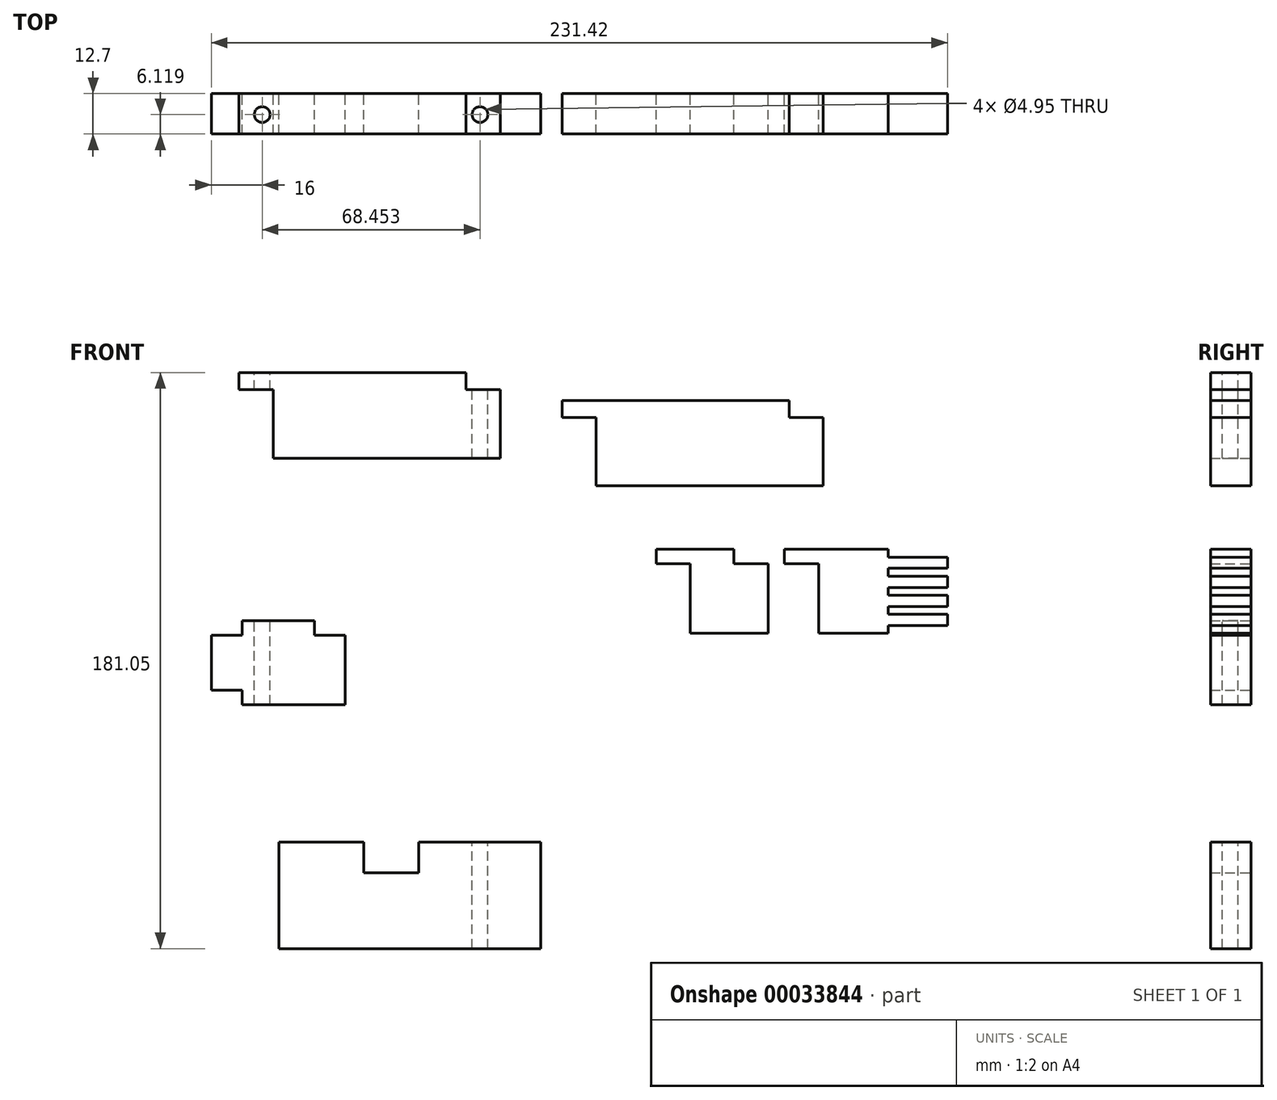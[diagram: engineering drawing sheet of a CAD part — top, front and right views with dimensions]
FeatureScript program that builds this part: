
annotation { "Feature Type Name" : "Feature", "Feature Type Description" : "" }
export const myFeature = defineFeature(function(context is Context, id is Id, definition is map)
    precondition{}
    {
        {
            var Q0;
            Q0=qCreatedBy(makeId("Front.planeOp"),FACE);
            var sketch = newSketch(context, id + "F0", { "sketchPlane" : qUnion([Q0])});
            skLineSegment(sketch, "E0.bottom", {"start": v(-99.87, -47.6) * mm, "end": v(-17.62, -47.6) * mm});
            skLineSegment(sketch, "E0.top", {"start": v(-99.87, -81.14) * mm, "end": v(-17.62, -81.14) * mm});
            skLineSegment(sketch, "E0.left", {"start": v(-99.87, -47.6) * mm, "end": v(-99.87, -81.14) * mm});
            skLineSegment(sketch, "E0.right", {"start": v(-17.62, -47.6) * mm, "end": v(-17.62, -81.14) * mm});
            skLineSegment(sketch, "E1.bottom", {"start": v(-112.5, 99.9) * mm, "end": v(-30.38, 99.9) * mm});
            skLineSegment(sketch, "E1.top", {"start": v(-112.5, 73.05) * mm, "end": v(-30.38, 73.05) * mm});
            skLineSegment(sketch, "E1.left", {"start": v(-112.5, 99.9) * mm, "end": v(-112.5, 73.05) * mm});
            skLineSegment(sketch, "E1.right", {"start": v(-30.38, 99.9) * mm, "end": v(-30.38, 73.05) * mm});
            skLineSegment(sketch, "E2", {"start": v(-112.5, 94.54) * mm, "end": v(-101.75, 94.54) * mm});
            skLineSegment(sketch, "E3", {"start": v(-101.75, 94.54) * mm, "end": v(-101.75, 77.27) * mm});
            skLineSegment(sketch, "E4", {"start": v(-101.75, 77.27) * mm, "end": v(-112.5, 77.27) * mm});
            skLineSegment(sketch, "E5", {"start": v(-30.38, 94.54) * mm, "end": v(-41.12, 94.54) * mm});
            skLineSegment(sketch, "E6", {"start": v(-41.12, 94.54) * mm, "end": v(-41.12, 77.27) * mm});
            skLineSegment(sketch, "E7", {"start": v(-41.12, 77.27) * mm, "end": v(-30.38, 77.27) * mm});
            skLineSegment(sketch, "E8.bottom", {"start": v(1.68, -53.97) * mm, "end": v(83.93, -53.97) * mm});
            skLineSegment(sketch, "E8.top", {"start": v(1.68, -87.5) * mm, "end": v(83.93, -87.5) * mm});
            skLineSegment(sketch, "E8.left", {"start": v(1.68, -53.97) * mm, "end": v(1.68, -87.5) * mm});
            skLineSegment(sketch, "E8.right", {"start": v(83.93, -53.97) * mm, "end": v(83.93, -87.5) * mm});
            skLineSegment(sketch, "E9.bottom", {"start": v(-10.94, 91.2) * mm, "end": v(71.17, 91.2) * mm});
            skLineSegment(sketch, "E9.top", {"start": v(-10.94, 64.34) * mm, "end": v(71.17, 64.34) * mm});
            skLineSegment(sketch, "E9.left", {"start": v(-10.94, 91.2) * mm, "end": v(-10.94, 64.34) * mm});
            skLineSegment(sketch, "E9.right", {"start": v(71.17, 91.2) * mm, "end": v(71.17, 64.34) * mm});
            skLineSegment(sketch, "E10", {"start": v(-10.94, 85.82) * mm, "end": v(-0.2, 85.82) * mm});
            skLineSegment(sketch, "E11", {"start": v(-0.2, 85.82) * mm, "end": v(-0.2, 68.56) * mm});
            skLineSegment(sketch, "E12", {"start": v(-0.2, 68.56) * mm, "end": v(-10.94, 68.56) * mm});
            skLineSegment(sketch, "E13", {"start": v(71.17, 85.82) * mm, "end": v(60.43, 85.82) * mm});
            skLineSegment(sketch, "E14", {"start": v(60.43, 85.82) * mm, "end": v(60.43, 68.56) * mm});
            skLineSegment(sketch, "E15", {"start": v(60.43, 68.56) * mm, "end": v(71.17, 68.56) * mm});
            skLineSegment(sketch, "E16.bottom", {"start": v(-111.54, 21.96) * mm, "end": v(-88.82, 21.96) * mm});
            skLineSegment(sketch, "E16.top", {"start": v(-111.54, -4.45) * mm, "end": v(-88.82, -4.45) * mm});
            skLineSegment(sketch, "E16.left", {"start": v(-111.54, 21.96) * mm, "end": v(-111.54, -4.45) * mm});
            skLineSegment(sketch, "E16.right", {"start": v(-88.82, 21.96) * mm, "end": v(-88.82, -4.45) * mm});
            skLineSegment(sketch, "E17.bottom", {"start": v(-88.82, 17.4) * mm, "end": v(-79.17, 17.4) * mm});
            skLineSegment(sketch, "E17.top", {"start": v(-88.82, 0.13) * mm, "end": v(-79.17, 0.13) * mm});
            skLineSegment(sketch, "E17.left", {"start": v(-88.82, 17.4) * mm, "end": v(-88.82, 0.13) * mm});
            skLineSegment(sketch, "E17.right", {"start": v(-79.17, 17.4) * mm, "end": v(-79.17, 0.13) * mm});
            skLineSegment(sketch, "E18", {"start": v(-0.2, 91.2) * mm, "end": v(-0.2, 64.34) * mm});
            skLineSegment(sketch, "E19", {"start": v(60.43, 91.2) * mm, "end": v(60.43, 64.34) * mm});
            skLineSegment(sketch, "E20.bottom", {"start": v(18.66, 44.37) * mm, "end": v(53.82, 44.37) * mm});
            skLineSegment(sketch, "E20.top", {"start": v(18.66, 17.95) * mm, "end": v(53.82, 17.95) * mm});
            skLineSegment(sketch, "E20.left", {"start": v(18.66, 44.37) * mm, "end": v(18.66, 17.95) * mm});
            skLineSegment(sketch, "E20.right", {"start": v(53.82, 44.37) * mm, "end": v(53.82, 17.95) * mm});
            skLineSegment(sketch, "E21.bottom", {"start": v(18.66, 39.8) * mm, "end": v(29.4, 39.8) * mm});
            skLineSegment(sketch, "E21.top", {"start": v(18.66, 22.52) * mm, "end": v(29.4, 22.52) * mm});
            skLineSegment(sketch, "E21.left", {"start": v(18.66, 39.8) * mm, "end": v(18.66, 22.52) * mm});
            skLineSegment(sketch, "E21.right", {"start": v(29.4, 39.8) * mm, "end": v(29.4, 22.52) * mm});
            skLineSegment(sketch, "E22.bottom", {"start": v(53.82, 39.8) * mm, "end": v(43.08, 39.8) * mm});
            skLineSegment(sketch, "E22.top", {"start": v(53.82, 22.52) * mm, "end": v(43.08, 22.52) * mm});
            skLineSegment(sketch, "E22.left", {"start": v(53.82, 39.8) * mm, "end": v(53.82, 22.52) * mm});
            skLineSegment(sketch, "E22.right", {"start": v(43.08, 39.8) * mm, "end": v(43.08, 22.52) * mm});
            skLineSegment(sketch, "E23.bottom", {"start": v(58.98, 39.8) * mm, "end": v(69.72, 39.8) * mm});
            skLineSegment(sketch, "E23.top", {"start": v(58.98, 22.52) * mm, "end": v(69.72, 22.52) * mm});
            skLineSegment(sketch, "E23.left", {"start": v(58.98, 39.8) * mm, "end": v(58.98, 22.52) * mm});
            skLineSegment(sketch, "E23.right", {"start": v(69.72, 39.8) * mm, "end": v(69.72, 22.52) * mm});
            skLineSegment(sketch, "E24.bottom", {"start": v(69.72, 44.37) * mm, "end": v(91.55, 44.37) * mm});
            skLineSegment(sketch, "E24.top", {"start": v(69.72, 17.95) * mm, "end": v(91.55, 17.95) * mm});
            skLineSegment(sketch, "E24.left", {"start": v(69.72, 44.37) * mm, "end": v(69.72, 17.95) * mm});
            skLineSegment(sketch, "E24.right", {"start": v(91.55, 44.37) * mm, "end": v(91.55, 17.95) * mm});
            skLineSegment(sketch, "E25.left", {"start": v(91.55, 44.37) * mm, "end": v(91.55, 38.1) * mm});
            skLineSegment(sketch, "E26.left", {"start": v(91.55, 32.2) * mm, "end": v(91.55, 28.51) * mm});
            skLineSegment(sketch, "E27.left", {"start": v(91.55, 23.69) * mm, "end": v(91.55, 20) * mm});
            skLineSegment(sketch, "E28.bottom", {"start": v(81.37, 17.95) * mm, "end": v(77.1, 17.95) * mm});
            skLineSegment(sketch, "E28.top", {"start": v(81.37, 9.97) * mm, "end": v(77.1, 9.97) * mm});
            skLineSegment(sketch, "E28.left", {"start": v(81.37, 17.95) * mm, "end": v(81.37, 9.97) * mm});
            skLineSegment(sketch, "E28.right", {"start": v(77.1, 17.95) * mm, "end": v(77.1, 9.97) * mm});
            skLineSegment(sketch, "E29.bottom", {"start": v(-111.54, 17.4) * mm, "end": v(-121.19, 17.4) * mm});
            skLineSegment(sketch, "E29.top", {"start": v(-111.54, 0.13) * mm, "end": v(-121.19, 0.13) * mm});
            skLineSegment(sketch, "E29.left", {"start": v(-111.54, 17.4) * mm, "end": v(-111.54, 0.13) * mm});
            skLineSegment(sketch, "E29.right", {"start": v(-121.19, 17.4) * mm, "end": v(-121.19, 0.13) * mm});
            skLineSegment(sketch, "E30.bottom", {"start": v(-73.2, -47.6) * mm, "end": v(-55.93, -47.6) * mm});
            skLineSegment(sketch, "E30.top", {"start": v(-73.2, -57.26) * mm, "end": v(-55.93, -57.26) * mm});
            skLineSegment(sketch, "E30.left", {"start": v(-73.2, -47.6) * mm, "end": v(-73.2, -57.26) * mm});
            skLineSegment(sketch, "E30.right", {"start": v(-55.93, -47.6) * mm, "end": v(-55.93, -57.26) * mm});
            skLineSegment(sketch, "E31.bottom", {"start": v(91.55, 41.9) * mm, "end": v(110.23, 41.9) * mm});
            skLineSegment(sketch, "E31.top", {"start": v(91.55, 38.38) * mm, "end": v(110.23, 38.38) * mm});
            skLineSegment(sketch, "E31.left", {"start": v(91.55, 41.9) * mm, "end": v(91.55, 38.38) * mm});
            skLineSegment(sketch, "E31.right", {"start": v(110.23, 41.9) * mm, "end": v(110.23, 38.38) * mm});
            skLineSegment(sketch, "E32.bottom", {"start": v(91.55, 35.91) * mm, "end": v(110.23, 35.91) * mm});
            skLineSegment(sketch, "E32.top", {"start": v(91.55, 32.4) * mm, "end": v(110.23, 32.4) * mm});
            skLineSegment(sketch, "E32.left", {"start": v(91.55, 35.91) * mm, "end": v(91.55, 32.4) * mm});
            skLineSegment(sketch, "E32.right", {"start": v(110.23, 35.91) * mm, "end": v(110.23, 32.4) * mm});
            skLineSegment(sketch, "E33.bottom", {"start": v(91.55, 29.93) * mm, "end": v(110.23, 29.93) * mm});
            skLineSegment(sketch, "E33.top", {"start": v(91.55, 26.4) * mm, "end": v(110.23, 26.4) * mm});
            skLineSegment(sketch, "E33.left", {"start": v(91.55, 29.93) * mm, "end": v(91.55, 26.4) * mm});
            skLineSegment(sketch, "E33.right", {"start": v(110.23, 29.93) * mm, "end": v(110.23, 26.4) * mm});
            skLineSegment(sketch, "E34.bottom", {"start": v(91.55, 20.42) * mm, "end": v(110.23, 20.42) * mm});
            skLineSegment(sketch, "E34.top", {"start": v(91.55, 23.94) * mm, "end": v(110.23, 23.94) * mm});
            skLineSegment(sketch, "E34.left", {"start": v(91.55, 20.42) * mm, "end": v(91.55, 23.94) * mm});
            skLineSegment(sketch, "E34.right", {"start": v(110.23, 20.42) * mm, "end": v(110.23, 23.94) * mm});
            skLineSegment(sketch, "E35", {"start": v(91.55, 44.37) * mm, "end": v(91.55, 41.9) * mm});
            skLineSegment(sketch, "E36", {"start": v(91.55, 38.38) * mm, "end": v(91.55, 35.91) * mm});
            skLineSegment(sketch, "E37", {"start": v(91.55, 32.4) * mm, "end": v(91.55, 29.93) * mm});
            skLineSegment(sketch, "E38", {"start": v(91.55, 26.4) * mm, "end": v(91.55, 23.94) * mm});
            skLineSegment(sketch, "E39", {"start": v(91.55, 20.42) * mm, "end": v(91.55, 17.95) * mm});
            skPoint(sketch, "E40.startSnap0", {"position": v(24.03, 39.8) * mm});
            skPoint(sketch, "E41.startSnap0", {"position": v(48.45, 22.52) * mm});
            skPoint(sketch, "E42.startSnap0", {"position": v(48.45, 39.8) * mm});
            skLineSegment(sketch, "E43", {"start": v(-101.75, 99.9) * mm, "end": v(-101.75, 73.05) * mm});
            skLineSegment(sketch, "E44", {"start": v(-41.12, 99.9) * mm, "end": v(-41.12, 73.05) * mm});
            skLineSegment(sketch, "E45", {"start": v(29.4, 44.37) * mm, "end": v(29.4, 17.95) * mm});
            skLineSegment(sketch, "E46", {"start": v(43.08, 44.37) * mm, "end": v(43.08, 17.95) * mm});
            skLineSegment(sketch, "E47", {"start": v(-111.54, 21.96) * mm, "end": v(-121.19, 21.96) * mm});
            skLineSegment(sketch, "E48", {"start": v(-121.19, 21.96) * mm, "end": v(-121.19, 17.4) * mm});
            skLineSegment(sketch, "E49", {"start": v(-121.19, 0.13) * mm, "end": v(-121.19, -4.45) * mm});
            skLineSegment(sketch, "E50", {"start": v(-121.19, -4.45) * mm, "end": v(-111.54, -4.45) * mm});
            skLineSegment(sketch, "E51", {"start": v(-88.82, -4.45) * mm, "end": v(-79.17, -4.45) * mm});
            skLineSegment(sketch, "E52", {"start": v(-79.17, -4.45) * mm, "end": v(-79.17, 0.13) * mm});
            skLineSegment(sketch, "E53", {"start": v(-88.82, 21.96) * mm, "end": v(-79.17, 21.96) * mm});
            skLineSegment(sketch, "E54", {"start": v(-79.17, 21.96) * mm, "end": v(-79.17, 17.4) * mm});
            skLineSegment(sketch, "E55", {"start": v(58.98, 22.52) * mm, "end": v(58.98, 17.95) * mm});
            skLineSegment(sketch, "E56", {"start": v(58.98, 17.95) * mm, "end": v(69.72, 17.95) * mm});
            skLineSegment(sketch, "E57", {"start": v(69.72, 44.37) * mm, "end": v(58.98, 44.37) * mm});
            skLineSegment(sketch, "E58", {"start": v(58.98, 44.37) * mm, "end": v(58.98, 39.8) * mm});
            skLineSegment(sketch, "E59", {"start": v(-112.5, 99.9) * mm, "end": v(-112.5, 94.54) * mm});
            skSolve(sketch);
        }
        {
            var Q0;
            {var subQ5=sQuery(id+"F0.wireOp",EDGE,"E9.bottom");var subQ7=sQuery(id+"F0.wireOp",EDGE,"E18");var subQ10=makeQuery(id+"F0.imprint","INTERSECT",VERTEX,{"derivedFrom":[subQ5,subQ7]});Q0=makeQuery(id+"F0.imprint","IMPRINT",FACE,{"disambiguationData":[TD([[makeQuery(id+"F0.imprint","IMPRINT",EDGE,{"disambiguationData":[TD([[subQ10,-1.0]])],"derivedFrom":subQ5}),-1.0]])]});}
            var Q1;
            {var subQ3=sQuery(id+"F0.wireOp",EDGE,"E10");Q1=makeQuery(id+"F0.imprint","IMPRINT",FACE,{"disambiguationData":[TD([[makeQuery(id+"F0.imprint","IMPRINT",EDGE,{"derivedFrom":subQ3}),1.0]])]});}
            var Q2;
            {var subQ2=sQuery(id+"F0.wireOp",EDGE,"E13");Q2=makeQuery(id+"F0.imprint","IMPRINT",FACE,{"disambiguationData":[TD([[makeQuery(id+"F0.imprint","IMPRINT",EDGE,{"derivedFrom":subQ2}),1.0]])]});}
            var Q3;
            {var subQ3=sQuery(id+"F0.wireOp",EDGE,"E15");Q3=makeQuery(id+"F0.imprint","IMPRINT",FACE,{"disambiguationData":[TD([[makeQuery(id+"F0.imprint","IMPRINT",EDGE,{"derivedFrom":subQ3}),-1.0]])]});}
            extrude(context, id + "F1", {"entities" : qUnion([Q0, Q1, Q2, Q3]), "depth" : 12.7 * mm});
        }
        {
            var Q0;
            Q0=makeQuery(id+"F0.imprint","IMPRINT",FACE,{"disambiguationData":[TD([[makeQuery(id+"F0.imprint","IMPRINT",EDGE,{"derivedFrom":sQuery(id+"F0.wireOp",EDGE,"E0.bottom")}),-1.0]])]});
            extrude(context, id + "F2", {"entities" : qUnion([Q0]), "depth" : 12.7 * mm});
        }
        {
            var Q0;
            {var subQ2=sQuery(id+"F0.wireOp",EDGE,"E16.bottom");Q0=makeQuery(id+"F0.imprint","IMPRINT",FACE,{"disambiguationData":[TD([[makeQuery(id+"F0.imprint","IMPRINT",EDGE,{"derivedFrom":subQ2}),-1.0]])]});}
            var Q1;
            Q1=makeQuery(id+"F0.imprint","IMPRINT",FACE,{"disambiguationData":[TD([[makeQuery(id+"F0.imprint","IMPRINT",EDGE,{"derivedFrom":sQuery(id+"F0.wireOp",EDGE,"E17.bottom")}),-1.0]])]});
            var Q2;
            Q2=makeQuery(id+"F0.imprint","IMPRINT",FACE,{"disambiguationData":[TD([[makeQuery(id+"F0.imprint","IMPRINT",EDGE,{"derivedFrom":sQuery(id+"F0.wireOp",EDGE,"E29.bottom")}),1.0]])]});
            var Q3;
            {var subQ1=sQuery(id+"F0.wireOp",EDGE,"E17.top");Q3=makeQuery(id+"F0.imprint","IMPRINT",FACE,{"disambiguationData":[TD([[makeQuery(id+"F0.imprint","IMPRINT",EDGE,{"derivedFrom":subQ1}),-1.0]])]});}
            extrude(context, id + "F3", {"entities" : qUnion([Q0, Q1, Q2, Q3]), "depth" : 12.7 * mm});
        }
        {
            var Q0;
            {var subQ3=sQuery(id+"F0.wireOp",EDGE,"E2");Q0=makeQuery(id+"F0.imprint","IMPRINT",FACE,{"disambiguationData":[TD([[makeQuery(id+"F0.imprint","IMPRINT",EDGE,{"derivedFrom":subQ3}),1.0]])]});}
            var Q1;
            {var subQ5=sQuery(id+"F0.wireOp",EDGE,"E1.bottom");var subQ7=sQuery(id+"F0.wireOp",EDGE,"E43");var subQ10=makeQuery(id+"F0.imprint","INTERSECT",VERTEX,{"derivedFrom":[subQ5,subQ7]});Q1=makeQuery(id+"F0.imprint","IMPRINT",FACE,{"disambiguationData":[TD([[makeQuery(id+"F0.imprint","IMPRINT",EDGE,{"disambiguationData":[TD([[subQ10,-1.0]])],"derivedFrom":subQ5}),-1.0]])]});}
            var Q2;
            {var subQ2=sQuery(id+"F0.wireOp",EDGE,"E5");Q2=makeQuery(id+"F0.imprint","IMPRINT",FACE,{"disambiguationData":[TD([[makeQuery(id+"F0.imprint","IMPRINT",EDGE,{"derivedFrom":subQ2}),1.0]])]});}
            var Q3;
            {var subQ3=sQuery(id+"F0.wireOp",EDGE,"E7");Q3=makeQuery(id+"F0.imprint","IMPRINT",FACE,{"disambiguationData":[TD([[makeQuery(id+"F0.imprint","IMPRINT",EDGE,{"derivedFrom":subQ3}),-1.0]])]});}
            extrude(context, id + "F4", {"entities" : qUnion([Q0, Q1, Q2, Q3]), "depth" : 12.7 * mm});
        }
        {
            var Q0;
            Q0=makeQuery(id+"F4.opExtrude","SWEPT_FACE",FACE,{"disambiguationData":[OSD([sQuery(id+"F0.wireOp",EDGE,"E1.bottom")])]});
            var sketch = newSketch(context, id + "F5", { "sketchPlane" : qUnion([Q0])});
            skCircle(sketch, "E60", {"center": v(-105.19, -6.58) * mm, "radius": 2.48 * mm});
            skCircle(sketch, "E61", {"center": v(-36.74, -6.58) * mm, "radius": 2.48 * mm});
            skSolve(sketch);
        }
        {
            var Q0;
            Q0=makeQuery(id+"F5.imprint","IMPRINT",FACE,{"disambiguationData":[TD([[makeQuery(id+"F5.imprint","IMPRINT",EDGE,{"derivedFrom":sQuery(id+"F5.wireOp",EDGE,"E60")}),1.0]])]});
            var Q1;
            Q1=makeQuery(id+"F5.imprint","IMPRINT",FACE,{"disambiguationData":[TD([[makeQuery(id+"F5.imprint","IMPRINT",EDGE,{"derivedFrom":sQuery(id+"F5.wireOp",EDGE,"E61")}),1.0]])]});
            extrude(context, id + "F6", {"entities" : qUnion([Q0, Q1]), "operationType" : NewBodyOperationType.REMOVE, "endBound" : BoundingType.THROUGH_ALL, "oppositeDirection" : true, "depth" : 25.4 * mm});
        }
        {
            var Q0;
            {var subQ4=sQuery(id+"F0.wireOp",EDGE,"E20.bottom");var subQ7=sQuery(id+"F0.wireOp",EDGE,"E45");var subQ11=makeQuery(id+"F0.imprint","INTERSECT",VERTEX,{"derivedFrom":[subQ4,subQ7]});Q0=makeQuery(id+"F0.imprint","IMPRINT",FACE,{"disambiguationData":[TD([[makeQuery(id+"F0.imprint","IMPRINT",EDGE,{"disambiguationData":[TD([[subQ11,-1.0]])],"derivedFrom":subQ4}),-1.0]])]});}
            var Q1;
            {var subQ3=sQuery(id+"F0.wireOp",EDGE,"E21.bottom");Q1=makeQuery(id+"F0.imprint","IMPRINT",FACE,{"disambiguationData":[TD([[makeQuery(id+"F0.imprint","IMPRINT",EDGE,{"derivedFrom":subQ3}),1.0]])]});}
            var Q2;
            {var subQ2=sQuery(id+"F0.wireOp",EDGE,"E22.bottom");Q2=makeQuery(id+"F0.imprint","IMPRINT",FACE,{"disambiguationData":[TD([[makeQuery(id+"F0.imprint","IMPRINT",EDGE,{"derivedFrom":subQ2}),1.0]])]});}
            var Q3;
            {var subQ3=sQuery(id+"F0.wireOp",EDGE,"E22.top");Q3=makeQuery(id+"F0.imprint","IMPRINT",FACE,{"disambiguationData":[TD([[makeQuery(id+"F0.imprint","IMPRINT",EDGE,{"derivedFrom":subQ3}),1.0]])]});}
            extrude(context, id + "F7", {"entities" : qUnion([Q0, Q1, Q2, Q3]), "depth" : 12.7 * mm});
        }
        {
            var Q0;
            {var subQ11=sQuery(id+"F0.wireOp",EDGE,"E24.bottom");Q0=makeQuery(id+"F0.imprint","IMPRINT",FACE,{"disambiguationData":[TD([[makeQuery(id+"F0.imprint","IMPRINT",EDGE,{"derivedFrom":subQ11}),-1.0]])]});}
            var Q1;
            {var subQ2=sQuery(id+"F0.wireOp",EDGE,"E25.top");Q1=makeQuery(id+"F0.imprint","IMPRINT",FACE,{"disambiguationData":[TD([[makeQuery(id+"F0.imprint","IMPRINT",EDGE,{"derivedFrom":subQ2}),1.0]])]});}
            var Q2;
            Q2=makeQuery(id+"F0.imprint","IMPRINT",FACE,{"disambiguationData":[TD([[makeQuery(id+"F0.imprint","IMPRINT",EDGE,{"derivedFrom":sQuery(id+"F0.wireOp",EDGE,"E26.bottom")}),-1.0]])]});
            var Q3;
            Q3=makeQuery(id+"F0.imprint","IMPRINT",FACE,{"disambiguationData":[TD([[makeQuery(id+"F0.imprint","IMPRINT",EDGE,{"derivedFrom":sQuery(id+"F0.wireOp",EDGE,"E27.bottom")}),-1.0]])]});
            var Q4;
            Q4=makeQuery(id+"F0.imprint","IMPRINT",FACE,{"disambiguationData":[TD([[makeQuery(id+"F0.imprint","IMPRINT",EDGE,{"derivedFrom":sQuery(id+"F0.wireOp",EDGE,"E28.bottom")}),1.0]])]});
            var Q5;
            Q5=makeQuery(id+"F0.imprint","IMPRINT",FACE,{"disambiguationData":[TD([[makeQuery(id+"F0.imprint","IMPRINT",EDGE,{"derivedFrom":sQuery(id+"F0.wireOp",EDGE,"E31.bottom")}),-1.0]])]});
            var Q6;
            Q6=makeQuery(id+"F0.imprint","IMPRINT",FACE,{"disambiguationData":[TD([[makeQuery(id+"F0.imprint","IMPRINT",EDGE,{"derivedFrom":sQuery(id+"F0.wireOp",EDGE,"E32.bottom")}),-1.0]])]});
            var Q7;
            {var subQ3=sQuery(id+"F0.wireOp",EDGE,"E33.bottom");Q7=makeQuery(id+"F0.imprint","IMPRINT",FACE,{"disambiguationData":[TD([[makeQuery(id+"F0.imprint","IMPRINT",EDGE,{"derivedFrom":subQ3}),-1.0]])]});}
            var Q8;
            {var subQ3=sQuery(id+"F0.wireOp",EDGE,"E34.bottom");Q8=makeQuery(id+"F0.imprint","IMPRINT",FACE,{"disambiguationData":[TD([[makeQuery(id+"F0.imprint","IMPRINT",EDGE,{"derivedFrom":subQ3}),1.0]])]});}
            var Q9;
            {var subQ2=sQuery(id+"F0.wireOp",EDGE,"E23.bottom");Q9=makeQuery(id+"F0.imprint","IMPRINT",FACE,{"disambiguationData":[TD([[makeQuery(id+"F0.imprint","IMPRINT",EDGE,{"derivedFrom":subQ2}),1.0]])]});}
            extrude(context, id + "F8", {"entities" : qUnion([Q0, Q1, Q2, Q3, Q4, Q5, Q6, Q7, Q8, Q9]), "depth" : 12.7 * mm});
        }
    });
